# Revit family: F_TTZNFS60x100_2DO_CAD_MULT_Prod
name_source: partatom
category: Detail Items
revit_build: Autodesk Revit 2015 (Build: 20140606_1530(x64)
units: mm (PartAtom-declared; Revit-internal decimal feet)

## types (2) — shared parameters
Density = 0.01 kg
Description = Screws
EPD = https://www.strongtie.eu
ETA / DoP = https://www.strongtie.eu
Manufacturer = Simpson Strong-Tie
Model = TTZNFS6.0X100
Model Disclaimer = Contact Simpson Strong-Tie Company  for more information
Model ID = 0289077240033297033376446180930740799796
Name = TTZNFS6.0X100
ObjectType = TTZNFS6.0X100
Product Material = Impreg®+
Product Type = Screws
Reference = 74497
Technical datasheet = https://www.strongtie.eu
URL = www.strongtie.eu
UniClass Number = Pr_20_29_76_98
UniClass Title = Wood screws

## per-type parameters (varying)
| type | _visiblefront | _visibletop |
| SST_TTZNFS6.0X100_Front | Yes | No |
| SST_TTZNFS6.0X100_Top | No | Yes |

## geometry (parser evidence)
native form markers: Sweep x2
no freeform markers — native parametric forms only
